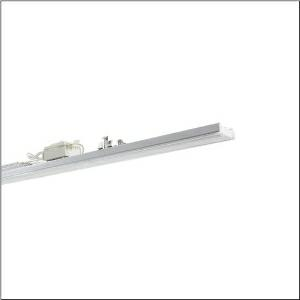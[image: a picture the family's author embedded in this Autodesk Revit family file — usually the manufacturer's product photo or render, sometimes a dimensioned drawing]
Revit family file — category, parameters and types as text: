
# Revit family: licross_r__21_recessed_ho_52tl11dv4l2s_4f4e
name_source: partatom
category: Lighting Fixtures
units: mm (PartAtom-declared; Revit-internal decimal feet)

## family parameters
Cut with Voids When Loaded = No
Host = Face
Light Source = No
Part Type = Normal
Room Calculation Point = No
Round Connector Dimension = Use Diameter
Shared = No

## types (1)
- --- (1 x LED, 22660 lm, 125.6 W, 4000K)
    Apparent Load = 126 VA
    CIE Flux Codes = 87 95 99 100 100
    Color Rendering = 80
    Color Temperature = 4000K
    Default Elevation = 1800 mm
    Description = Licross® 21 Recessed HO, luminaire insert, of sheet steel, galvanised, coil coated, white, length: 2.250mm, width: 66mm, height: 67mm, LED rated luminous flux: 22.660lm, light colour: 840, control gear: DALI 2, with plug, 5-pole, with phase selection, mains connection: 220..240V, AC, 50/60Hz, rated input power: 126W, halogen-free wiring, primary light control with lens, of plastic, primary optical cover: cover, of PMMA, light emission: direct distribution, primary light characteristic: symmetric, protection rating (complete): IP40, insulation class (complete): insulation class I (protective earthing), certification: CE, ENEC, VDE, UKCA, protection symbol: D if used in an environment without relevant dust loads with corresponding accessories, impact resistance: IK06, permissible ambient temperature for indoor applications: -40..+30°C, corresponds to IFS (International Featured Standards) requirements for safety and quality in the food industry, reducing of maximum allowable ambient temperature of 5°C with ceiling mounting, LABS conformity tested according to VDMA 24364:2018-05, packaging unit: 1 piece
    Height = 58 mm
    Lamp = 1 x LED
    Lamp Light Flux = 22660 lm
    Lamp Power = 125.6 W
    Lamp count = 1
    Length = 2250 mm
    Luminous efficacy = 180 lm/W
    Manufacturer = Siteco
    ModVariant = No
    Model = 52TL11DV4L2S
    Mounting Place = Ceiling
    Mounting Type = Pendant
    Number of Poles = 1
    OnlyDefault = Yes
    Power Factor = 1
    Product Name = Licross® 21 Recessed HO
    Product group = luminaire insert
    ProductGroupID = 902
    Protection Class = Protection class I
    Protection Degree = IP 40
    RLX_Detail_Level = 1
    RLX_Emergency_Light_Flux = 0 lm
    RLX_Emergency_Type = 0
    RLX_Emergency_Type_DB = No
    RlxData = <blob elided: 29641 chars, md5=95a995b7>
    Socket = socket
    Standby Power = 0 W
    System Light Flux = 22659 lm
    System Power = 126 W
    Type Comments = factory setting: luminous flux: 100 % | dim-lin: 254 | 489 mA
    Type Image = l_1296930.jpg
    URL = http://relux.com
    VarID = @adj_127420
    Voltage = 0 V
    Weight = 0.00 kg
    Width = 66 mm

## geometry (parser evidence)
native form markers: Blend x4, Sweep x10
no freeform markers — native parametric forms only
